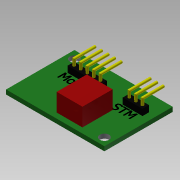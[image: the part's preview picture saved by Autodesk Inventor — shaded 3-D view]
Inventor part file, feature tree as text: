
AUTODESK INVENTOR PART (.ipt)
format: ipt  version: 2015 SP1 (Build 190203100, 203)  size: 171,008 bytes
history: native  units: mm
features: sketch x3, extrude x3, sweep x1
ambient origin geometry x8: Origin, YZ Plane, XZ Plane, XY Plane, X Axis, Y Axis, Z Axis, Center Point
bodies: Solid1 (feature_tree)
feature tree (7):
  sketch  "Sketch1"  dims[d0=38.0mm d1=26.416mm]
  extrude  "Extrusion1"  Depth=26.416mm
  extrude  "Extrusion2"  Depth=3.5mm
  extrude  "Extrusion3"  Depth=4.1mm
  sweep  "Sweep1"
  sketch  "Sketch3"  dims[d4=3.0mm d5=3.0mm d6=3.0mm d7=3.0mm d8=1.0mm d9=4.572mm d10=4.69mm d11=50.0mm d13=2.54mm d14=10.0mm d16=10.0mm d18=1.27mm d19=1.27mm d20=1.27mm d21=1.27mm d22=1.0mm d23=11.176mm d24=30.0mm d26=2.54mm d27=10.0mm d29=10.0mm d31=1.27mm d33=1.27mm d34=9.96mm d35=11.66mm d36=3.74mm d37=1.7mm d38=0.0mm d39=8.62mm d40=0.0mm d41=4.1mm d42=0.0mm d43=6.15mm d44=7.87mm d45=0.0mm d46=0.0mm]
  sketch  "Sketch2"  dims[d2=3.5mm d3=3.5mm]
